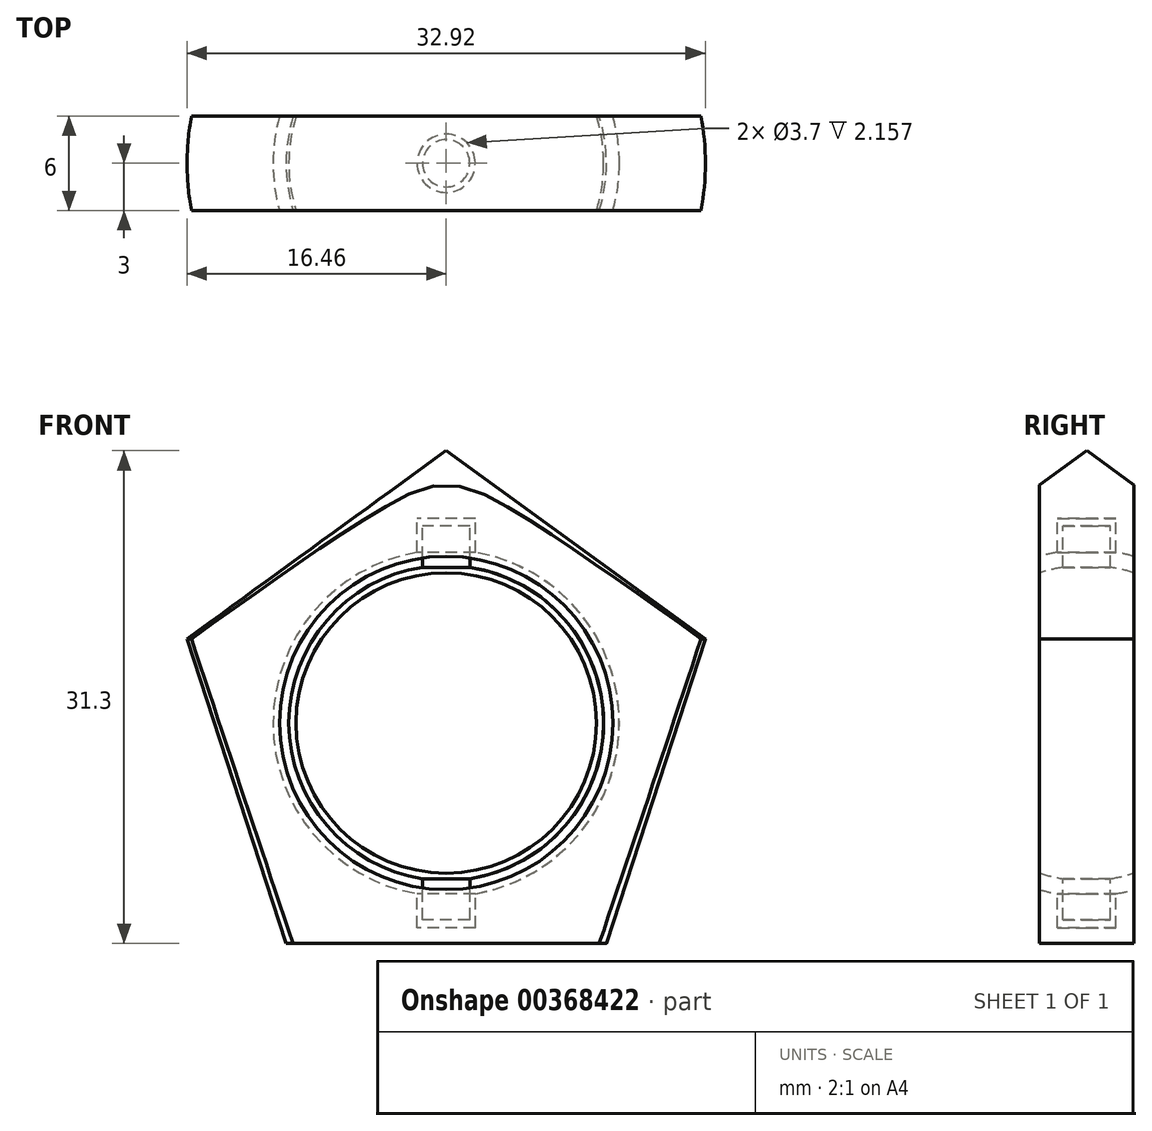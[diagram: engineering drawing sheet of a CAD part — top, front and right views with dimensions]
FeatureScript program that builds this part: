
annotation { "Feature Type Name" : "Feature", "Feature Type Description" : "" }
export const myFeature = defineFeature(function(context is Context, id is Id, definition is map)
    precondition{}
    {
        {
            var Q0;
            Q0=qCreatedBy(makeId("Front.planeOp"),FACE);
            var sketch = newSketch(context, id + "F0", { "sketchPlane" : qUnion([Q0])});
            skCircle(sketch, "E0.cCircle", {"center": v(0, 0) * mm, "radius": 14 * mm, "construction": true});
            skLineSegment(sketch, "E0.0", {"start": v(0, 17.3) * mm, "end": v(16.46, 5.35) * mm});
            skLineSegment(sketch, "E0.1", {"start": v(16.46, 5.35) * mm, "end": v(10.17, -14) * mm});
            skLineSegment(sketch, "E0.2", {"start": v(10.17, -14) * mm, "end": v(-10.17, -14) * mm});
            skLineSegment(sketch, "E0.3", {"start": v(-10.17, -14) * mm, "end": v(-16.46, 5.35) * mm});
            skLineSegment(sketch, "E0.4", {"start": v(-16.46, 5.35) * mm, "end": v(0, 17.3) * mm});
            skPoint(sketch, "E0.0.midPoint", {"position": v(8.23, 11.33) * mm});
            skCircle(sketch, "E1", {"center": v(0, 0) * mm, "radius": 11 * mm});
            skCircle(sketch, "E2", {"center": v(0, 0) * mm, "radius": 0.13 * mm});
            skCircle(sketch, "E3", {"center": v(0, 0) * mm, "radius": 10 * mm});
            skLineSegment(sketch, "E4.bottom", {"start": v(1.85, 13) * mm, "end": v(-1.85, 13) * mm});
            skLineSegment(sketch, "E4.top", {"start": v(1.85, -13) * mm, "end": v(-1.85, -13) * mm});
            skLineSegment(sketch, "E4.left", {"start": v(1.85, 13) * mm, "end": v(1.85, -13) * mm});
            skLineSegment(sketch, "E4.right", {"start": v(-1.85, 13) * mm, "end": v(-1.85, -13) * mm});
            skLineSegment(sketch, "E5.bottom", {"start": v(1.5, 12.5) * mm, "end": v(-1.5, 12.5) * mm});
            skLineSegment(sketch, "E5.top", {"start": v(1.5, -12.5) * mm, "end": v(-1.5, -12.5) * mm});
            skLineSegment(sketch, "E5.left", {"start": v(1.5, 12.5) * mm, "end": v(1.5, -12.5) * mm});
            skLineSegment(sketch, "E5.right", {"start": v(-1.5, 12.5) * mm, "end": v(-1.5, -12.5) * mm});
            skSolve(sketch);
        }
        {
            var Q0;
            Q0=qCreatedBy(makeId("Front.planeOp"),FACE);
            var sketch = newSketch(context, id + "F1", { "sketchPlane" : qUnion([Q0])});
            skLineSegment(sketch, "E6.0", {"start": v(-16.46, 5.35) * mm, "end": v(0, 17.3) * mm});
            skLineSegment(sketch, "E7.1", {"start": v(0, 17.3) * mm, "end": v(16.46, 5.35) * mm});
            skPoint(sketch, "E8.2", {"position": v(1.85, 13) * mm});
            skLineSegment(sketch, "E9.0", {"start": v(-10.17, -14) * mm, "end": v(-16.46, 5.35) * mm});
            skLineSegment(sketch, "E10.0", {"start": v(10.17, -14) * mm, "end": v(-10.17, -14) * mm});
            skLineSegment(sketch, "E11.0", {"start": v(16.46, 5.35) * mm, "end": v(10.17, -14) * mm});
            skLineSegment(sketch, "E12.0", {"start": v(1.85, 13) * mm, "end": v(1.85, 10.84) * mm});
            skArc(sketch, "E13.1", {"start": v(-1.5, 9.89) * mm, "mid": v(-10, 0) * mm, "end": v(-1.5, -9.89) * mm});
            skArc(sketch, "E14.0", {"start": v(-1.5, 9.89) * mm, "mid": v(-10, 0.18) * mm, "end": v(-1.85, -9.83) * mm});
            skArc(sketch, "E15.0", {"start": v(-1.85, 10.84) * mm, "mid": v(-11, 0) * mm, "end": v(-1.85, -10.84) * mm});
            skPoint(sketch, "E16.0", {"position": v(1.5, -12.5) * mm});
            skPoint(sketch, "E17.0", {"position": v(-1.5, -12.5) * mm});
            skLineSegment(sketch, "E18.0", {"start": v(1.5, -12.5) * mm, "end": v(-1.5, -12.5) * mm});
            skLineSegment(sketch, "E19.0", {"start": v(1.85, -13) * mm, "end": v(-1.85, -13) * mm});
            skLineSegment(sketch, "E20.0", {"start": v(-1.5, 12.5) * mm, "end": v(-1.5, 9.89) * mm});
            skLineSegment(sketch, "E21.0", {"start": v(-1.85, 13) * mm, "end": v(-1.85, 10.84) * mm});
            skLineSegment(sketch, "E22.0", {"start": v(1.5, 12.5) * mm, "end": v(1.5, 9.89) * mm});
            skLineSegment(sketch, "E23.0", {"start": v(1.85, 13) * mm, "end": v(-1.85, 13) * mm});
            skLineSegment(sketch, "E24.0", {"start": v(1.5, 12.5) * mm, "end": v(-1.5, 12.5) * mm});
            skPoint(sketch, "E25.0", {"position": v(8.23, 11.33) * mm});
            skLineSegment(sketch, "E26.trimOffspring", {"start": v(-1.5, -9.89) * mm, "end": v(-1.5, -12.5) * mm});
            skLineSegment(sketch, "E27.trimOffspring", {"start": v(-1.85, -10.84) * mm, "end": v(-1.85, -13) * mm});
            skLineSegment(sketch, "E28.trimOffspring", {"start": v(1.5, -9.89) * mm, "end": v(1.5, -12.5) * mm});
            skLineSegment(sketch, "E29.trimOffspring", {"start": v(1.85, -10.84) * mm, "end": v(1.85, -13) * mm});
            skArc(sketch, "E30.trimOffspring", {"start": v(1.5, -9.89) * mm, "mid": v(10, 0) * mm, "end": v(1.5, 9.89) * mm});
            skArc(sketch, "E31.trimOffspring", {"start": v(1.85, -10.84) * mm, "mid": v(11, 0) * mm, "end": v(1.85, 10.84) * mm});
            skArc(sketch, "E32.trimOffspring", {"start": v(1.85, -9.83) * mm, "mid": v(10, 0.18) * mm, "end": v(1.5, 9.89) * mm});
            skSolve(sketch);
        }
        {
            var Q0;
            Q0=qCreatedBy(makeId("Front.planeOp"),FACE);
            var sketch = newSketch(context, id + "F2", { "sketchPlane" : qUnion([Q0])});
            skArc(sketch, "E33.0", {"start": v(1.85, -10.84) * mm, "mid": v(11, 0) * mm, "end": v(1.85, 10.84) * mm});
            skArc(sketch, "E34.0", {"start": v(1.85, -9.83) * mm, "mid": v(10, 0.18) * mm, "end": v(1.5, 9.89) * mm});
            skPoint(sketch, "E35.0", {"position": v(1.5, -9.89) * mm});
            skLineSegment(sketch, "E36.0", {"start": v(1.5, -9.89) * mm, "end": v(1.5, -12.5) * mm});
            skLineSegment(sketch, "E37.0", {"start": v(1.85, -10.84) * mm, "end": v(1.85, -13) * mm});
            skLineSegment(sketch, "E38.0", {"start": v(1.85, -13) * mm, "end": v(0, -13) * mm});
            skLineSegment(sketch, "E39.0", {"start": v(1.5, -12.5) * mm, "end": v(0, -12.5) * mm});
            skLineSegment(sketch, "E40.0", {"start": v(0, 17.3) * mm, "end": v(16.46, 5.35) * mm});
            skLineSegment(sketch, "E41.0", {"start": v(1.85, 13) * mm, "end": v(0, 13) * mm});
            skLineSegment(sketch, "E42.0", {"start": v(1.5, 12.5) * mm, "end": v(0, 12.5) * mm});
            skLineSegment(sketch, "E43.0", {"start": v(1.5, 12.5) * mm, "end": v(1.5, 9.89) * mm});
            skLineSegment(sketch, "E44.0", {"start": v(1.85, 13) * mm, "end": v(1.85, 10.84) * mm});
            skLineSegment(sketch, "E45.0", {"start": v(10.17, -14) * mm, "end": v(0, -14) * mm});
            skLineSegment(sketch, "E46.0", {"start": v(16.46, 5.35) * mm, "end": v(10.17, -14) * mm});
            skArc(sketch, "E47.0", {"start": v(1.5, -9.89) * mm, "mid": v(10, 0) * mm, "end": v(1.5, 9.89) * mm});
            skLineSegment(sketch, "E48", {"start": v(0, 17.3) * mm, "end": v(0, 13) * mm});
            skPoint(sketch, "E49.0.end.orphan", {"position": v(-16.46, 5.35) * mm});
            skPoint(sketch, "E49.0.start.orphan", {"position": v(-10.17, -14) * mm});
            skPoint(sketch, "E50.orphan", {"position": v(-1.5, 9.89) * mm});
            skPoint(sketch, "E51.0.end.orphan", {"position": v(-1.85, -10.84) * mm});
            skPoint(sketch, "E51.0.start.orphan", {"position": v(-1.85, 10.84) * mm});
            skPoint(sketch, "E52.0.start.orphan", {"position": v(-1.85, 13) * mm});
            skPoint(sketch, "E53.0.start.orphan", {"position": v(-1.5, 12.5) * mm});
            skPoint(sketch, "E54.0.end.orphan", {"position": v(-1.5, -12.5) * mm});
            skPoint(sketch, "E54.0.start.orphan", {"position": v(-1.5, -9.89) * mm});
            skPoint(sketch, "E55.0.end.orphan", {"position": v(-1.85, -13) * mm});
            skPoint(sketch, "E56.0.start.orphan", {"position": v(-1.85, -9.83) * mm});
            skLineSegment(sketch, "E57.trimOffspring", {"start": v(0, -13) * mm, "end": v(0, -14) * mm});
            skLineSegment(sketch, "E58.trimOffspring", {"start": v(0, 12.5) * mm, "end": v(0, -12.5) * mm});
            skSolve(sketch);
        }
        {
            var Q0;
            {var subQ1=sQuery(id+"F2.wireOp",EDGE,"E36.0");Q0=makeQuery(id+"F2.imprint","IMPRINT",FACE,{"disambiguationData":[TD([[makeQuery(id+"F2.imprint","IMPRINT",EDGE,{"derivedFrom":subQ1}),-1.0]])]});}
            var Q1;
            Q1=makeQuery(id+"F2.imprint","IMPRINT",FACE,{"disambiguationData":[TD([[makeQuery(id+"F2.imprint","IMPRINT",EDGE,{"derivedFrom":sQuery(id+"F2.wireOp",EDGE,"E33.0")}),-1.0]])]});
            var Q2;
            Q2=sQuery(id+"F2.wireOp",EDGE,"E48");
            revolve(context, id + "F3", {"entities" : qUnion([Q0, Q1]), "axis" : qUnion([Q2]), "revolveType" : RevolveType.FULL});
        }
        {
            var Q0;
            Q0=qCreatedBy(makeId("Right.planeOp"),FACE);
            var sketch = newSketch(context, id + "F4", { "sketchPlane" : qUnion([Q0])});
            skLineSegment(sketch, "E59.bottom", {"start": v(-21.22, 20.9) * mm, "end": v(-3, 20.9) * mm});
            skLineSegment(sketch, "E59.top", {"start": v(-21.22, -19.1) * mm, "end": v(-3, -19.1) * mm});
            skLineSegment(sketch, "E59.left", {"start": v(-21.22, 20.9) * mm, "end": v(-21.22, -19.1) * mm});
            skLineSegment(sketch, "E59.right", {"start": v(-3, 20.9) * mm, "end": v(-3, -19.1) * mm});
            skLineSegment(sketch, "E60", {"start": v(-3, 0) * mm, "end": v(0, 0) * mm});
            skLineSegment(sketch, "E61", {"start": v(0, 0) * mm, "end": v(-3, 0) * mm});
            skLineSegment(sketch, "E62.bottom", {"start": v(3, 21.07) * mm, "end": v(17.54, 21.07) * mm});
            skLineSegment(sketch, "E62.top", {"start": v(3, -19.87) * mm, "end": v(17.54, -19.87) * mm});
            skLineSegment(sketch, "E62.left", {"start": v(3, 21.07) * mm, "end": v(3, -19.87) * mm});
            skLineSegment(sketch, "E62.right", {"start": v(17.54, 21.07) * mm, "end": v(17.54, -19.87) * mm});
            skLineSegment(sketch, "E63", {"start": v(0, 0) * mm, "end": v(3, 0) * mm});
            skPoint(sketch, "E64.orphan", {"position": v(-9.17, 0) * mm});
            skSolve(sketch);
        }
        {
            var Q0;
            {var subQ3=sQuery(id+"F4.wireOp",EDGE,"E62.bottom");Q0=makeQuery(id+"F4.imprint","IMPRINT",FACE,{"disambiguationData":[TD([[makeQuery(id+"F4.imprint","IMPRINT",EDGE,{"derivedFrom":subQ3}),-1.0]])]});}
            var Q1;
            {var subQ1=sQuery(id+"F4.wireOp",EDGE,"E59.bottom");Q1=makeQuery(id+"F4.imprint","IMPRINT",FACE,{"disambiguationData":[TD([[makeQuery(id+"F4.imprint","IMPRINT",EDGE,{"derivedFrom":subQ1}),-1.0]])]});}
            extrude(context, id + "F5", {"entities" : qUnion([Q0, Q1]), "operationType" : NewBodyOperationType.REMOVE, "endBound" : BoundingType.SYMMETRIC, "oppositeDirection" : true, "depth" : 60 * mm});
        }
    });
